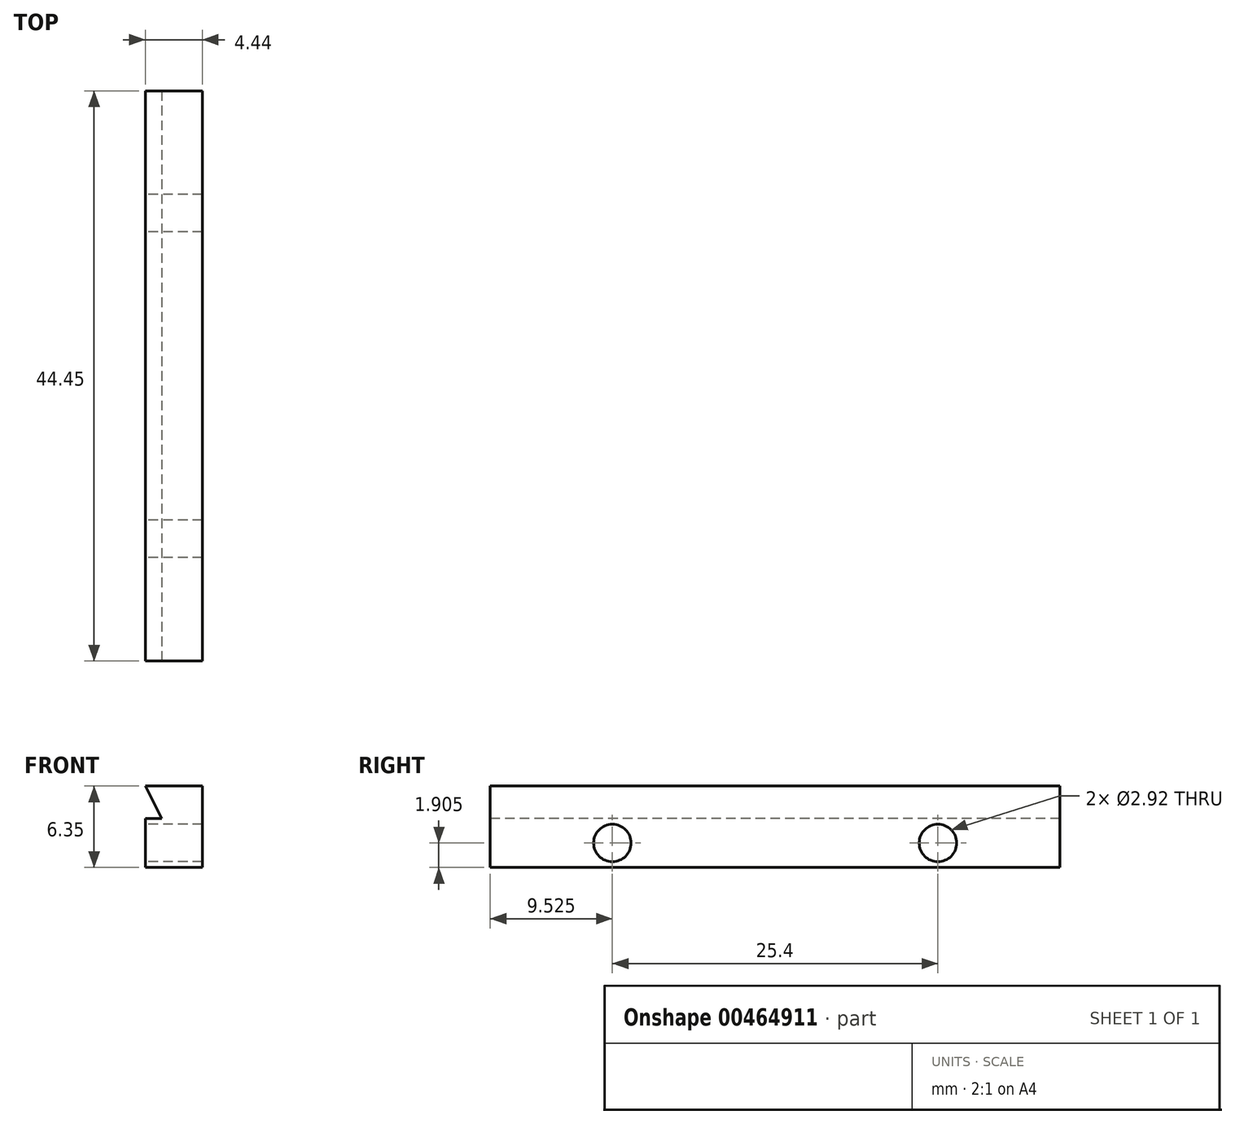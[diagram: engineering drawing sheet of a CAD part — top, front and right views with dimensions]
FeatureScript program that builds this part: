
annotation { "Feature Type Name" : "Feature", "Feature Type Description" : "" }
export const myFeature = defineFeature(function(context is Context, id is Id, definition is map)
    precondition{}
    {
        {
            var Q0;
            Q0=qCreatedBy(makeId("Right.planeOp"),FACE);
            var sketch = newSketch(context, id + "F0", { "sketchPlane" : qUnion([Q0])});
            skLineSegment(sketch, "E0.bottom", {"start": v(31.75, 6.35) * mm, "end": v(-19.05, 6.35) * mm});
            skLineSegment(sketch, "E0.top", {"start": v(19.05, -6.35) * mm, "end": v(-31.75, -6.35) * mm});
            skPoint(sketch, "E0.middle", {"position": v(0, 0) * mm});
            skLineSegment(sketch, "E1", {"start": v(-31.75, -6.35) * mm, "end": v(-19.05, 6.35) * mm});
            skLineSegment(sketch, "E2", {"start": v(31.75, 6.35) * mm, "end": v(19.05, -6.35) * mm});
            skSolve(sketch);
        }
        {
            var Q0;
            Q0=qSketchRegion(id+"F0",true);
            extrude(context, id + "F1", {"entities" : qUnion([Q0]), "endBound" : BoundingType.SYMMETRIC, "depth" : 20.07 * mm});
        }
        {
            var Q0;
            Q0=qCreatedBy(makeId("Front.planeOp"),FACE);
            var sketch = newSketch(context, id + "F2", { "sketchPlane" : qUnion([Q0])});
            skLineSegment(sketch, "E3", {"start": v(0, 1.15) * mm, "end": v(0, -10.33) * mm, "construction": true});
            skLineSegment(sketch, "E4", {"start": v(-5.59, -6.35) * mm, "end": v(-6.86, -3.81) * mm});
            skLineSegment(sketch, "E5", {"start": v(-6.86, -3.81) * mm, "end": v(6.86, -3.81) * mm});
            skLineSegment(sketch, "E6", {"start": v(6.86, -3.81) * mm, "end": v(5.59, -6.35) * mm});
            skLineSegment(sketch, "E7", {"start": v(5.59, -6.35) * mm, "end": v(-5.59, -6.35) * mm});
            skLineSegment(sketch, "E8", {"start": v(-14.86, 0) * mm, "end": v(21.63, 0) * mm, "construction": true});
            skLineSegment(sketch, "E9.MirrorCS", {"start": v(-5.59, 6.35) * mm, "end": v(-6.86, 3.81) * mm});
            skLineSegment(sketch, "E10.MirrorCS", {"start": v(-6.86, 3.81) * mm, "end": v(6.86, 3.81) * mm});
            skLineSegment(sketch, "E11.MirrorCS", {"start": v(5.59, 6.35) * mm, "end": v(-5.59, 6.35) * mm});
            skLineSegment(sketch, "E12.MirrorCS", {"start": v(6.86, 3.81) * mm, "end": v(5.59, 6.35) * mm});
            skSolve(sketch);
        }
        {
            var Q0;
            Q0=qSketchRegion(id+"F2",true);
            extrude(context, id + "F3", {"entities" : qUnion([Q0]), "operationType" : NewBodyOperationType.REMOVE, "endBound" : BoundingType.SYMMETRIC, "oppositeDirection" : true, "depth" : 152.4 * mm});
        }
        {
            var Q0;
            Q0=qCreatedBy(makeId("Front.planeOp"),FACE);
            var sketch = newSketch(context, id + "F4", { "sketchPlane" : qUnion([Q0])});
            skLineSegment(sketch, "E13.top", {"start": v(10.03, 0) * mm, "end": v(5.59, 0) * mm});
            skLineSegment(sketch, "E13.right", {"start": v(5.59, 6.35) * mm, "end": v(5.59, 0) * mm});
            skLineSegment(sketch, "E14", {"start": v(5.59, 6.35) * mm, "end": v(-11.39, 6.35) * mm});
            skLineSegment(sketch, "E15", {"start": v(-11.39, 6.35) * mm, "end": v(-11.39, -9.57) * mm});
            skLineSegment(sketch, "E16", {"start": v(-11.39, -9.57) * mm, "end": v(16.26, -9.57) * mm});
            skLineSegment(sketch, "E17", {"start": v(16.26, -9.57) * mm, "end": v(10.03, 0) * mm});
            skSolve(sketch);
        }
        {
            var Q0;
            Q0 = qSketchRegion(id + "F4", true);
            extrude(context, id + "F5", {"entities" : qUnion([Q0]), "operationType" : NewBodyOperationType.REMOVE, "endBound" : BoundingType.SYMMETRIC, "oppositeDirection" : true, "depth" : 152.4 * mm});
        }
        {
            var Q0;
            Q0=makeQuery(id+"F5.boolean.opBoolean","COPY",FACE,{"derivedFrom":makeQuery(id+"F5.opExtrude","SWEPT_FACE",FACE,{"disambiguationData":[OSD([sQuery(id+"F4.wireOp",EDGE,"E13.right")])]})});
            var sketch = newSketch(context, id + "F6", { "sketchPlane" : qUnion([Q0])});
            skCircle(sketch, "E18", {"center": v(-15.88, 1.9) * mm, "radius": 1.9 * mm});
            skCircle(sketch, "E19", {"center": v(9.53, 1.9) * mm, "radius": 1.9 * mm});
            skSolve(sketch);
        }
        {
            var Q0;
            Q0=sQuery(id+"F6.wireOp",VERTEX,"E18.center");
            var Q1;
            Q1=sQuery(id+"F6.wireOp",VERTEX,"E19.center");
            var Q2;
            Q2=makeQuery(id+"F1.opExtrude","SWEPT_BODY",BODY,{"disambiguationData":[OSD([sQuery(id+"F0.wireOp",EDGE,"E0.bottom"),sQuery(id+"F0.wireOp",EDGE,"E0.top"),sQuery(id+"F0.wireOp",EDGE,"E1"),sQuery(id+"F0.wireOp",EDGE,"E2")])]});
            hole(context, id + "F7", {"style" : HoleStyle.SIMPLE, "endStyle" : HoleEndStyle.BLIND, "holeDiameter" : 2.92 * mm, "holeDepth" : 8.25 * mm, "tappedDepth" : 6.35 * mm, "tapClearance" : 3, "locations" : qUnion([Q0, Q1]), "scope" : qUnion([Q2])});
        }
        {
            var Q0;
            Q0=makeQuery(id+"F1.opExtrude","CAP_FACE",FACE,{"disambiguationData":[OSD([sQuery(id+"F0.wireOp",EDGE,"E0.bottom"),sQuery(id+"F0.wireOp",EDGE,"E0.top"),sQuery(id+"F0.wireOp",EDGE,"E1"),sQuery(id+"F0.wireOp",EDGE,"E2")])],"isStart":false});
            var sketch = newSketch(context, id + "F8", { "sketchPlane" : qUnion([Q0])});
            skLineSegment(sketch, "E20", {"start": v(-25.4, 0) * mm, "end": v(-19.05, 6.35) * mm});
            skLineSegment(sketch, "E21", {"start": v(-19.05, 6.35) * mm, "end": v(-19.05, 0) * mm});
            skLineSegment(sketch, "E22", {"start": v(-19.05, 0) * mm, "end": v(-25.4, 0) * mm});
            skLineSegment(sketch, "E23", {"start": v(25.4, 0) * mm, "end": v(25.4, 6.35) * mm});
            skLineSegment(sketch, "E24", {"start": v(25.4, 6.35) * mm, "end": v(31.75, 6.35) * mm});
            skLineSegment(sketch, "E25", {"start": v(31.75, 6.35) * mm, "end": v(25.4, 0) * mm});
            skSolve(sketch);
        }
        {
            var Q0;
            Q0 = qSketchRegion(id + "F8", true);
            extrude(context, id + "F9", {"entities" : qUnion([Q0]), "operationType" : NewBodyOperationType.REMOVE, "endBound" : BoundingType.THROUGH_ALL, "oppositeDirection" : true, "depth" : 25.4 * mm});
        }
    });
